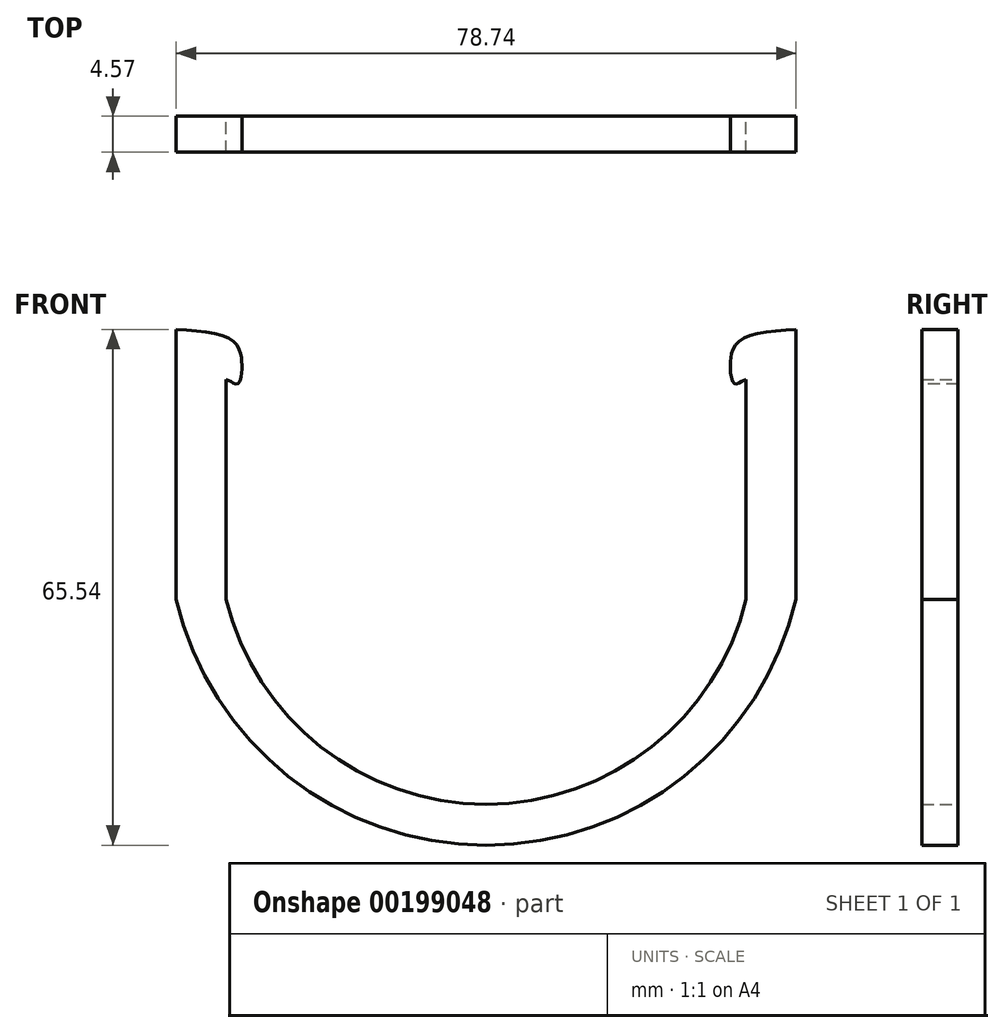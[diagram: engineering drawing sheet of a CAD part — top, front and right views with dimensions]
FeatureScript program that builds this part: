
annotation { "Feature Type Name" : "Feature", "Feature Type Description" : "" }
export const myFeature = defineFeature(function(context is Context, id is Id, definition is map)
    precondition{}
    {
        {
            var Q0;
            Q0=qCreatedBy(makeId("Front.planeOp"),FACE);
            var sketch = newSketch(context, id + "F0", { "sketchPlane" : qUnion([Q0])});
            skLineSegment(sketch, "E0", {"start": v(0, 34.3) * mm, "end": v(0, 0) * mm});
            skLineSegment(sketch, "E1", {"start": v(6.35, 27.94) * mm, "end": v(6.35, 0) * mm});
            skFitSpline(sketch, "E2", {"points": [v(0, 34.3) * mm, v(6.72, 33.15) * mm, v(8.12, 31.41) * mm, v(8.34, 30.02) * mm, v(8.31, 28.77) * mm, v(7.94, 27.48) * mm, v(7.44, 27.4) * mm, v(6.9, 27.68) * mm, v(6.35, 27.94) * mm], "startDerivative": vector(30.07, -1.9) * mm, "endDerivative": vector(-6.94, 3.13) * mm});
            skLineSegment(sketch, "E3", {"start": v(39.37, 45.4) * mm, "end": v(39.37, -26.56) * mm, "construction": true});
            skLineSegment(sketch, "E4.MirrorCS", {"start": v(72.4, 27.94) * mm, "end": v(72.4, 0) * mm});
            skLineSegment(sketch, "E5.MirrorCS", {"start": v(78.74, 34.3) * mm, "end": v(78.74, 0) * mm});
            skFitSpline(sketch, "E6.MirrorCS", {"points": [v(78.74, 34.3) * mm, v(72.02, 33.15) * mm, v(70.62, 31.41) * mm, v(70.4, 30.02) * mm, v(70.43, 28.77) * mm, v(70.8, 27.48) * mm, v(71.3, 27.4) * mm, v(71.85, 27.68) * mm, v(72.4, 27.94) * mm], "startDerivative": vector(-30.07, -1.9) * mm, "endDerivative": vector(6.94, 3.13) * mm});
            skArc(sketch, "E7", {"start": v(6.35, 0) * mm, "mid": v(39.37, -26.03) * mm, "end": v(72.4, 0) * mm});
            skArc(sketch, "E8", {"start": v(0, 0) * mm, "mid": v(39.37, -31.25) * mm, "end": v(78.74, 0) * mm});
            skSolve(sketch);
        }
        {
            var Q0;
            Q0=makeQuery(id+"F0.imprint","IMPRINT",FACE,{"disambiguationData":[TD([[makeQuery(id+"F0.imprint","IMPRINT",EDGE,{"derivedFrom":sQuery(id+"F0.wireOp",EDGE,"E0")}),1.0]])]});
            var sketch = newSketch(context, id + "F1", { "sketchPlane" : qUnion([Q0])});
            skSolve(sketch);
        }
        {
            var Q0;
            Q0=makeQuery(id+"F0.imprint","IMPRINT",FACE,{"disambiguationData":[TD([[makeQuery(id+"F0.imprint","IMPRINT",EDGE,{"derivedFrom":sQuery(id+"F0.wireOp",EDGE,"E0")}),1.0]])]});
            var Q1;
            Q1=makeQuery(id+"F1.imprint","IMPRINT",FACE,{"disambiguationData":[TD([[makeQuery(id+"F1.imprint","IMPRINT",EDGE,{"derivedFrom":makeQuery(id+"F0.imprint","IMPRINT",EDGE,{"derivedFrom":sQuery(id+"F0.wireOp",EDGE,"E0")})}),1.0]])]});
            extrude(context, id + "F2", {"entities" : qUnion([Q0, Q1]), "depth" : 4.57 * mm});
        }
    });
